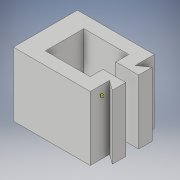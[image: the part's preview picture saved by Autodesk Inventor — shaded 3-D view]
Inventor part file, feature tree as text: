
AUTODESK INVENTOR PART (.ipt)
format: ipt  version: 2017 (Build 210142000, 142)  size: 116,736 bytes
history: native  units: in
note: dims shown in document units (in); Inventor stores cm internally (conversion verified against a paired STEP export)
features: extrude x1, sketch x1
ambient origin geometry x8: Origin, YZ Plane, XZ Plane, XY Plane, X Axis, Y Axis, Z Axis, Center Point
bodies: Solid1 (feature_tree)
feature tree (2):
  extrude  "Extrusion1"  Depth=0.4724in
  sketch  "Sketch1"  dims[d3=0.061in d4=0.4724in d5=0.1181in d9=0.3937in d10=0.0in d17=0.2441in d18=0.3937in d19=0.2362in d20=0.5335in d21=0.0394in d22=0.3779in d26=0.3779in d27=0.2756in d28=0.2756in]
